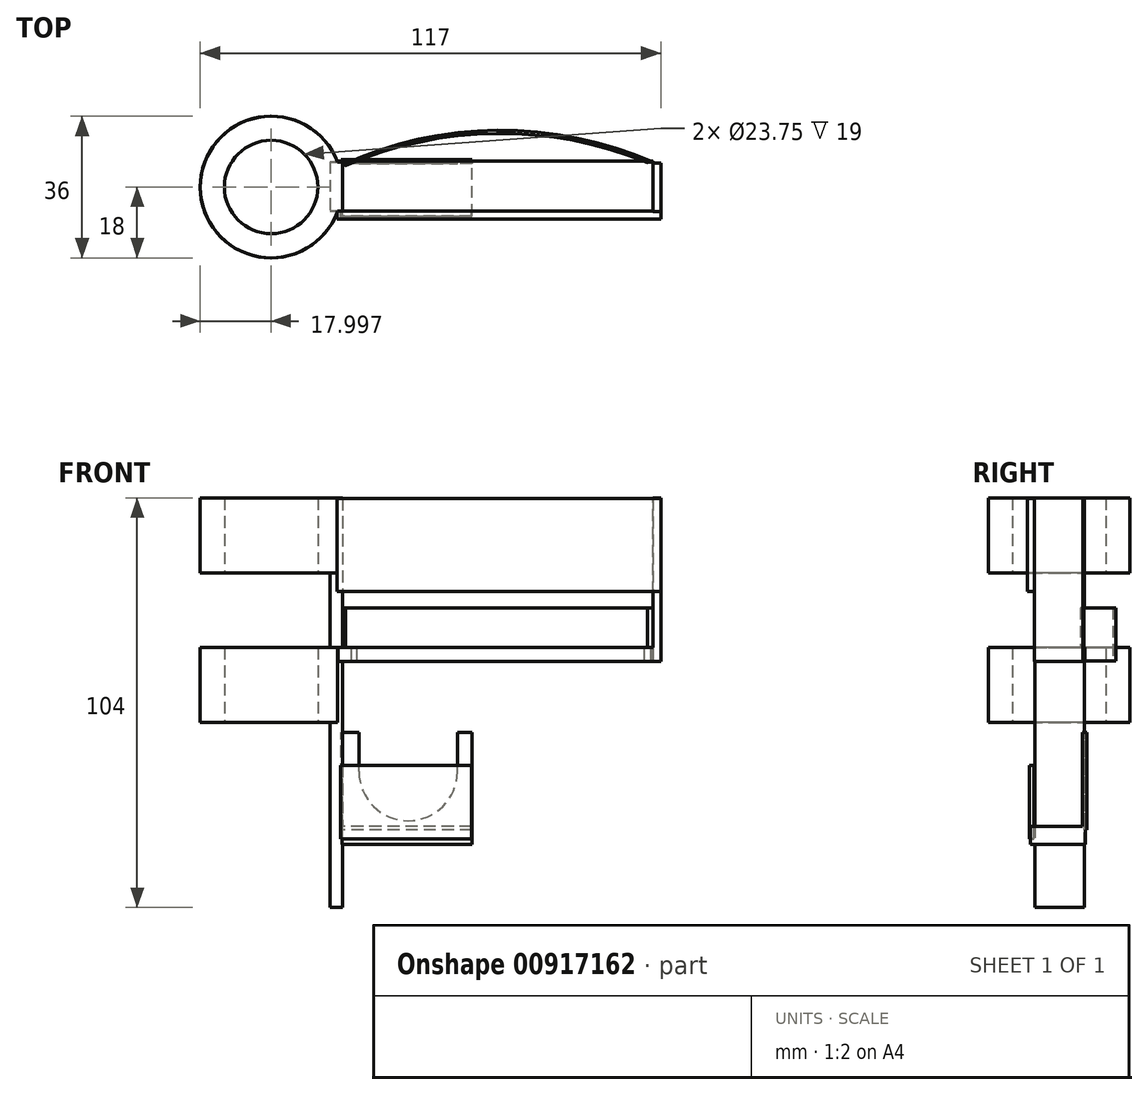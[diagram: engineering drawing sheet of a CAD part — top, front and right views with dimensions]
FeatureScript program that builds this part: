
annotation { "Feature Type Name" : "Feature", "Feature Type Description" : "" }
export const myFeature = defineFeature(function(context is Context, id is Id, definition is map)
    precondition{}
    {
        {
            var Q0;
            Q0=qCreatedBy(makeId("Top.planeOp"),FACE);
            var sketch = newSketch(context, id + "F0", { "sketchPlane" : qUnion([Q0])});
            skCircle(sketch, "E0", {"center": v(-64.56, 2.48) * mm, "radius": 18 * mm});
            skSolve(sketch);
        }
        {
            var Q0;
            Q0=qSketchRegion(id+"F0",true);
            extrude(context, id + "F1", {"entities" : qUnion([Q0]), "depth" : 8 * mm, "offsetDistance" : 25 * mm});
        }
        {
            var Q0;
            Q0=makeQuery(id+"F1.opExtrude","CAP_FACE",FACE,{"disambiguationData":[OSD([sQuery(id+"F0.wireOp",EDGE,"E0")])],"isStart":false});
            var sketch = newSketch(context, id + "F2", { "sketchPlane" : qUnion([Q0])});
            skCircle(sketch, "E1", {"center": v(-64.56, 2.48) * mm, "radius": 11.88 * mm});
            skSolve(sketch);
        }
        {
            var Q0;
            Q0=makeQuery(id+"F2.imprint","IMPRINT",FACE,{"disambiguationData":[TD([[makeQuery(id+"F2.imprint","IMPRINT",EDGE,{"derivedFrom":sQuery(id+"F2.wireOp",EDGE,"E1")}),-1.0]])]});
            extrude(context, id + "F3", {"entities" : qUnion([Q0]), "operationType" : NewBodyOperationType.ADD, "depth" : 96 * mm, "offsetDistance" : 25 * mm});
        }
        {
            var Q0;
            Q0=makeQuery(id+"F3.opExtrude","CAP_FACE",FACE,{"disambiguationData":[OSD([sQuery(id+"F0.wireOp",EDGE,"E0"),sQuery(id+"F2.wireOp",EDGE,"E1")])],"isStart":false});
            cPlane(context, id + "F4", {"entities" : qUnion([Q0]), "cplaneType" : CPlaneType.OFFSET, "offset" : 19 * mm, "oppositeDirection" : true, "width" : 150 * mm, "height" : 150 * mm});
        }
        {
            var Q0;
            Q0=qCreatedBy(id+"F4.planeOp",FACE);
            cPlane(context, id + "F5", {"entities" : qUnion([Q0]), "cplaneType" : CPlaneType.OFFSET, "offset" : 19 * mm, "oppositeDirection" : true, "width" : 150 * mm, "height" : 150 * mm});
        }
        {
            var Q0;
            Q0=qCreatedBy(id+"F5.planeOp",FACE);
            cPlane(context, id + "F6", {"entities" : qUnion([Q0]), "cplaneType" : CPlaneType.OFFSET, "offset" : 19 * mm, "oppositeDirection" : true, "width" : 150 * mm, "height" : 150 * mm});
        }
        {
            var Q0;
            Q0=qCreatedBy(id+"F5.planeOp",FACE);
            var sketch = newSketch(context, id + "F7", { "sketchPlane" : qUnion([Q0])});
            skLineSegment(sketch, "E2.bottom", {"start": v(-117.1, -27.67) * mm, "end": v(-2.84, -27.67) * mm});
            skLineSegment(sketch, "E2.top", {"start": v(-117.1, 43.37) * mm, "end": v(-2.84, 43.37) * mm});
            skLineSegment(sketch, "E2.left", {"start": v(-117.1, -27.67) * mm, "end": v(-117.1, 43.37) * mm});
            skLineSegment(sketch, "E2.right", {"start": v(-2.84, -27.67) * mm, "end": v(-2.84, 43.37) * mm});
            skSolve(sketch);
        }
        {
            var Q0;
            Q0=qSketchRegion(id+"F7",true);
            extrude(context, id + "F8", {"entities" : qUnion([Q0]), "operationType" : NewBodyOperationType.REMOVE, "depth" : 19 * mm, "offsetDistance" : 25 * mm});
        }
        {
            var Q0;
            Q0=qCreatedBy(id+"F6.planeOp",FACE);
            var sketch = newSketch(context, id + "F9", { "sketchPlane" : qUnion([Q0])});
            skLineSegment(sketch, "E3.bottom", {"start": v(-134.77, -40.96) * mm, "end": v(8.12, -40.96) * mm});
            skLineSegment(sketch, "E3.top", {"start": v(-134.77, 48.4) * mm, "end": v(8.12, 48.4) * mm});
            skLineSegment(sketch, "E3.left", {"start": v(-134.77, -40.96) * mm, "end": v(-134.77, 48.4) * mm});
            skLineSegment(sketch, "E3.right", {"start": v(8.12, -40.96) * mm, "end": v(8.12, 48.4) * mm});
            skSolve(sketch);
        }
        {
            var Q0;
            Q0=qSketchRegion(id+"F9",true);
            extrude(context, id + "F10", {"entities" : qUnion([Q0]), "operationType" : NewBodyOperationType.REMOVE, "oppositeDirection" : true, "depth" : 19 * mm, "offsetDistance" : 25 * mm});
        }
        {
            var Q0;
            Q0=qCreatedBy(makeId("Top.planeOp"),FACE);
            var sketch = newSketch(context, id + "F11", { "sketchPlane" : qUnion([Q0])});
            skLineSegment(sketch, "E4.bottom", {"start": v(-47.03, 8.87) * mm, "end": v(-50.03, 8.87) * mm});
            skLineSegment(sketch, "E4.top", {"start": v(-47.03, -3.63) * mm, "end": v(-50.03, -3.63) * mm});
            skLineSegment(sketch, "E5.bottom", {"start": v(-49.55, -3.63) * mm, "end": v(-46.43, -3.63) * mm});
            skLineSegment(sketch, "E5.top", {"start": v(-49.55, 8.87) * mm, "end": v(-46.43, 8.87) * mm});
            skLineSegment(sketch, "E5.left", {"start": v(-49.55, -3.63) * mm, "end": v(-49.55, 8.87) * mm});
            skLineSegment(sketch, "E5.right", {"start": v(-46.43, -3.63) * mm, "end": v(-46.43, 8.87) * mm});
            skSolve(sketch);
        }
        {
            var Q0;
            Q0=qSketchRegion(id+"F11",true);
            extrude(context, id + "F12", {"entities" : qUnion([Q0]), "depth" : 104 * mm, "offsetDistance" : 25 * mm});
        }
        {
            var Q0;
            Q0=makeQuery(id+"F3.opExtrude","CAP_FACE",FACE,{"disambiguationData":[OSD([sQuery(id+"F0.wireOp",EDGE,"E0"),sQuery(id+"F2.wireOp",EDGE,"E1")])],"isStart":false});
            cPlane(context, id + "F13", {"entities" : qUnion([Q0]), "cplaneType" : CPlaneType.OFFSET, "offset" : 38 * mm, "oppositeDirection" : true, "width" : 150 * mm, "height" : 150 * mm});
        }
        {
            var Q0;
            Q0=qCreatedBy(id+"F13.planeOp",FACE);
            var sketch = newSketch(context, id + "F14", { "sketchPlane" : qUnion([Q0])});
            skLineSegment(sketch, "E6.bottom", {"start": v(-47.56, -3.77) * mm, "end": v(32.44, -3.77) * mm});
            skLineSegment(sketch, "E6.top", {"start": v(-47.56, 9.06) * mm, "end": v(32.44, 9.06) * mm});
            skLineSegment(sketch, "E6.left", {"start": v(-47.56, -3.77) * mm, "end": v(-47.56, 9.06) * mm});
            skLineSegment(sketch, "E6.right", {"start": v(32.44, -3.77) * mm, "end": v(32.44, 9.06) * mm});
            skSolve(sketch);
        }
        {
            var Q0;
            Q0=qSketchRegion(id+"F14",true);
            extrude(context, id + "F15", {"entities" : qUnion([Q0]), "operationType" : NewBodyOperationType.ADD, "oppositeDirection" : true, "depth" : 3.5 * mm, "offsetDistance" : 25 * mm});
        }
        {
            var Q0;
            Q0=makeQuery(id+"F15.opExtrude","SWEPT_FACE",FACE,{"disambiguationData":[OSD([sQuery(id+"F14.wireOp",EDGE,"E6.right")])]});
            var sketch = newSketch(context, id + "F16", { "sketchPlane" : qUnion([Q0])});
            skLineSegment(sketch, "E7.bottom", {"start": v(-3.77, 62.5) * mm, "end": v(8.53, 62.5) * mm});
            skLineSegment(sketch, "E7.top", {"start": v(-3.77, 104) * mm, "end": v(8.53, 104) * mm});
            skLineSegment(sketch, "E7.left", {"start": v(-3.77, 62.5) * mm, "end": v(-3.77, 104) * mm});
            skLineSegment(sketch, "E7.right", {"start": v(8.53, 62.5) * mm, "end": v(8.53, 104) * mm});
            skSolve(sketch);
        }
        {
            var Q0;
            {var subQ0=sQuery(id+"F16.wireOp",EDGE,"E7.top");Q0=makeQuery(id+"F16.imprint","IMPRINT",FACE,{"disambiguationData":[TD([[makeQuery(id+"F16.imprint","IMPRINT",EDGE,{"derivedFrom":subQ0}),-1.0]])]});}
            var Q1;
            {var subQ0=sQuery(id+"F16.wireOp",EDGE,"E7.bottom");Q1=makeQuery(id+"F16.imprint","IMPRINT",FACE,{"disambiguationData":[TD([[makeQuery(id+"F16.imprint","IMPRINT",EDGE,{"derivedFrom":subQ0}),1.0]])]});}
            extrude(context, id + "F17", {"entities" : qUnion([Q0, Q1]), "operationType" : NewBodyOperationType.ADD, "depth" : 2 * mm, "offsetDistance" : 25 * mm});
        }
        {
            var Q0;
            Q0=makeQuery(id+"F12.opExtrude","SWEPT_FACE",FACE,{"disambiguationData":[OSD([sQuery(id+"F11.wireOp",EDGE,"E5.bottom")])]});
            var sketch = newSketch(context, id + "F18", { "sketchPlane" : qUnion([Q0])});
            skLineSegment(sketch, "E8.bottom", {"start": v(-47.77, 80.27) * mm, "end": v(34.43, 80.27) * mm});
            skLineSegment(sketch, "E8.top", {"start": v(-47.77, 103.88) * mm, "end": v(34.43, 103.88) * mm});
            skLineSegment(sketch, "E8.left", {"start": v(-47.77, 80.27) * mm, "end": v(-47.77, 103.88) * mm});
            skLineSegment(sketch, "E8.right", {"start": v(34.43, 80.27) * mm, "end": v(34.43, 103.88) * mm});
            skSolve(sketch);
        }
        {
            var Q0;
            Q0=qSketchRegion(id+"F18",true);
            extrude(context, id + "F19", {"entities" : qUnion([Q0]), "operationType" : NewBodyOperationType.ADD, "depth" : 2 * mm, "offsetDistance" : 25 * mm});
        }
        {
            var Q0;
            Q0=qCreatedBy(makeId("Top.planeOp"),FACE);
            cPlane(context, id + "F20", {"entities" : qUnion([Q0]), "cplaneType" : CPlaneType.OFFSET, "offset" : 62.6 * mm, "width" : 150 * mm, "height" : 150 * mm});
        }
        {
            var Q0;
            Q0=qCreatedBy(id+"F20.planeOp",FACE);
            var sketch = newSketch(context, id + "F21", { "sketchPlane" : qUnion([Q0])});
            skArc(sketch, "E9", {"start": v(32.5, 8.77) * mm, "mid": v(-7.15, 16.88) * mm, "end": v(-46.63, 8.01) * mm});
            skArc(sketch, "E10", {"start": v(31.06, 8.73) * mm, "mid": v(-7.35, 16.1) * mm, "end": v(-45.6, 7.94) * mm});
            skLineSegment(sketch, "E11", {"start": v(-46.63, 8.01) * mm, "end": v(-45.6, 7.94) * mm});
            skLineSegment(sketch, "E12", {"start": v(31.06, 8.73) * mm, "end": v(32.5, 8.77) * mm});
            skLineSegment(sketch, "E13", {"start": v(32.5, 8.77) * mm, "end": v(34.01, 8.1) * mm});
            skLineSegment(sketch, "E14", {"start": v(34.01, 8.1) * mm, "end": v(34.01, 7.49) * mm});
            skLineSegment(sketch, "E15", {"start": v(34.01, 7.49) * mm, "end": v(33.25, 7.49) * mm});
            skLineSegment(sketch, "E16", {"start": v(33.25, 7.49) * mm, "end": v(32.5, 8.23) * mm});
            skLineSegment(sketch, "E17", {"start": v(32.5, 8.23) * mm, "end": v(31.06, 8.73) * mm});
            skSolve(sketch);
        }
        {
            var Q0;
            Q0=makeQuery(id+"F21.imprint","IMPRINT",FACE,{"disambiguationData":[TD([[makeQuery(id+"F21.imprint","IMPRINT",EDGE,{"derivedFrom":sQuery(id+"F21.wireOp",EDGE,"E9")}),1.0]])]});
            extrude(context, id + "F22", {"entities" : qUnion([Q0]), "operationType" : NewBodyOperationType.ADD, "depth" : 13.5 * mm, "offsetDistance" : 25 * mm});
        }
        {
            var Q0;
            Q0=qCreatedBy(makeId("Front.planeOp"),FACE);
            cPlane(context, id + "F23", {"entities" : qUnion([Q0]), "cplaneType" : CPlaneType.OFFSET, "offset" : 3.9 * mm, "width" : 150 * mm, "height" : 150 * mm});
        }
        {
            var Q0;
            Q0=qCreatedBy(makeId("Front.planeOp"),FACE);
            cPlane(context, id + "F24", {"entities" : qUnion([Q0]), "cplaneType" : CPlaneType.OFFSET, "offset" : 9.5 * mm, "oppositeDirection" : true, "width" : 150 * mm, "height" : 150 * mm});
        }
        {
            var Q0;
            Q0=makeQuery(id+"F10.boolean.opBoolean","SPLIT",BODY,{"disambiguationData":[OD(1.0)],"derivedFrom":makeQuery(id+"F8.boolean.opBoolean","SPLIT",BODY,{"disambiguationData":[OD(0.0)],"derivedFrom":makeQuery(id+"F1.opExtrude","SWEPT_BODY",BODY,{"disambiguationData":[OSD([sQuery(id+"F0.wireOp",EDGE,"E0")])]})})});
            deleteBodies(context, id + "F25", {"entities" : qUnion([Q0])});
        }
        {
            var Q0;
            Q0=makeQuery(id+"F17.boolean.opBoolean","MERGE",FACE,{"derivedFrom":[makeQuery(id+"F15.opExtrude","CAP_FACE",FACE,{"disambiguationData":[OSD([sQuery(id+"F14.wireOp",EDGE,"E6.bottom"),sQuery(id+"F14.wireOp",EDGE,"E6.top"),sQuery(id+"F14.wireOp",EDGE,"E6.left"),sQuery(id+"F14.wireOp",EDGE,"E6.right")])],"isStart":false}),makeQuery(id+"F17.opExtrude","SWEPT_FACE",FACE,{"disambiguationData":[OSD([sQuery(id+"F16.wireOp",EDGE,"E7.bottom")])]})]});
            cPlane(context, id + "F26", {"entities" : qUnion([Q0]), "cplaneType" : CPlaneType.OFFSET, "offset" : 46.5 * mm, "width" : 150 * mm, "height" : 150 * mm});
        }
        {
            var Q0;
            Q0=qCreatedBy(id+"F26.planeOp",FACE);
            var sketch = newSketch(context, id + "F27", { "sketchPlane" : qUnion([Q0])});
            skLineSegment(sketch, "E18.bottom", {"start": v(-46.54, 4.84) * mm, "end": v(-13.54, 4.84) * mm});
            skLineSegment(sketch, "E18.top", {"start": v(-46.54, -9.16) * mm, "end": v(-13.54, -9.16) * mm});
            skLineSegment(sketch, "E18.left", {"start": v(-46.54, 4.84) * mm, "end": v(-46.54, -9.16) * mm});
            skLineSegment(sketch, "E18.right", {"start": v(-13.54, 4.84) * mm, "end": v(-13.54, -9.16) * mm});
            skSolve(sketch);
        }
        {
            var Q0;
            Q0=qSketchRegion(id+"F27",true);
            extrude(context, id + "F28", {"entities" : qUnion([Q0]), "operationType" : NewBodyOperationType.ADD, "oppositeDirection" : true, "depth" : 4.6 * mm, "offsetDistance" : 25 * mm});
        }
        {
            var Q0;
            Q0=qCreatedBy(id+"F24.planeOp",FACE);
            var sketch = newSketch(context, id + "F29", { "sketchPlane" : qUnion([Q0])});
            skLineSegment(sketch, "E19.bottom", {"start": v(-13.53, 19.7) * mm, "end": v(-46.84, 19.7) * mm});
            skLineSegment(sketch, "E19.top", {"start": v(-13.53, 44.49) * mm, "end": v(-46.84, 44.49) * mm});
            skLineSegment(sketch, "E19.left", {"start": v(-13.53, 19.7) * mm, "end": v(-13.53, 44.49) * mm});
            skLineSegment(sketch, "E19.right", {"start": v(-46.84, 19.7) * mm, "end": v(-46.84, 44.49) * mm});
            skCircle(sketch, "E20", {"center": v(-29.75, 34.47) * mm, "radius": 12.5 * mm});
            skLineSegment(sketch, "E21", {"start": v(-17.25, 34.47) * mm, "end": v(-17.25, 44.49) * mm});
            skLineSegment(sketch, "E22", {"start": v(-42.25, 34.47) * mm, "end": v(-42.25, 44.49) * mm});
            skSolve(sketch);
        }
        {
            var Q0;
            Q0=makeQuery(id+"F29.imprint","IMPRINT",FACE,{"disambiguationData":[TD([[makeQuery(id+"F29.imprint","IMPRINT",EDGE,{"derivedFrom":sQuery(id+"F29.wireOp",EDGE,"E19.bottom")}),-1.0]])]});
            extrude(context, id + "F30", {"entities" : qUnion([Q0]), "operationType" : NewBodyOperationType.ADD, "depth" : 1.1 * mm, "offsetDistance" : 25 * mm});
        }
        {
            var Q0;
            Q0=qCreatedBy(id+"F23.planeOp",FACE);
            var sketch = newSketch(context, id + "F31", { "sketchPlane" : qUnion([Q0])});
            skLineSegment(sketch, "E23.bottom", {"start": v(-13.64, 17.36) * mm, "end": v(-46.91, 17.36) * mm});
            skLineSegment(sketch, "E23.top", {"start": v(-13.64, 36.04) * mm, "end": v(-46.91, 36.04) * mm});
            skLineSegment(sketch, "E23.left", {"start": v(-13.64, 17.36) * mm, "end": v(-13.64, 36.04) * mm});
            skLineSegment(sketch, "E23.right", {"start": v(-46.91, 17.36) * mm, "end": v(-46.91, 36.04) * mm});
            skSolve(sketch);
        }
        {
            var Q0;
            Q0=qSketchRegion(id+"F31",true);
            extrude(context, id + "F32", {"entities" : qUnion([Q0]), "operationType" : NewBodyOperationType.ADD, "depth" : 1.2 * mm, "offsetDistance" : 25 * mm});
        }
    });
